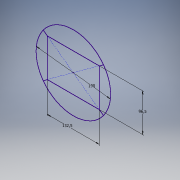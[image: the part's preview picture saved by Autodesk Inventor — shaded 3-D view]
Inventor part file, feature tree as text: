
AUTODESK INVENTOR PART (.ipt)
format: ipt  version: 2016 (Build 200138000, 138)  size: 86,016 bytes
history: native  units: mm
features: sketch x1
ambient origin geometry x8: Origin, YZ Plane, XZ Plane, XY Plane, X Axis, Y Axis, Z Axis, Center Point
feature tree (1):
  sketch  "Sketch2"  dims[d10=132.5mm d11=96.5mm d12=190.0mm]
